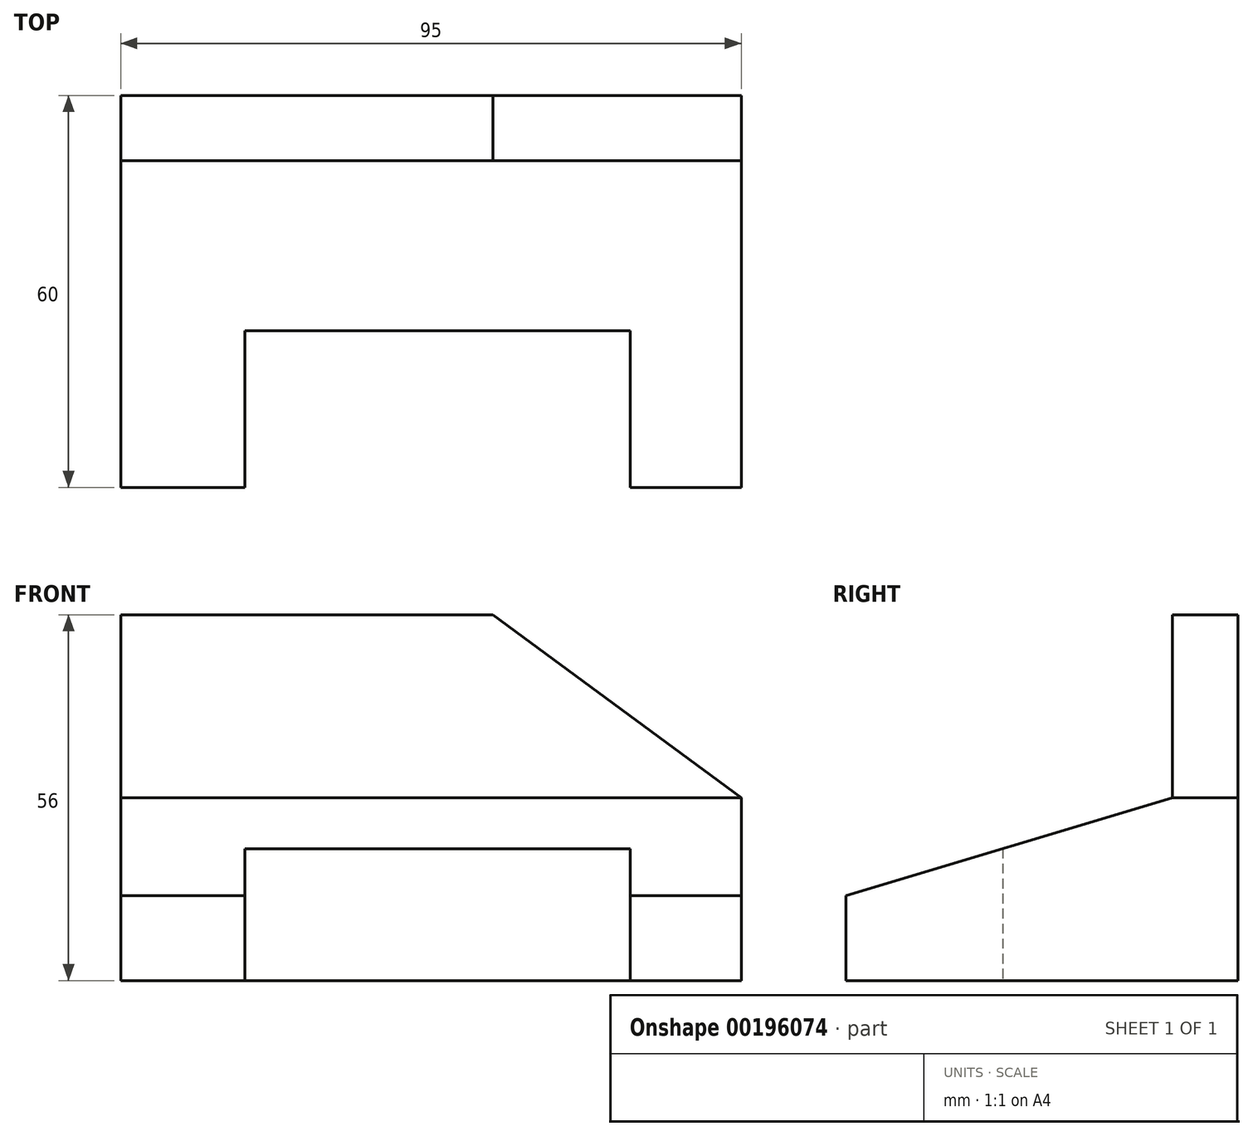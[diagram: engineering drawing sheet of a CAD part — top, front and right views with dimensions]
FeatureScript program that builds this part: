
annotation { "Feature Type Name" : "Feature", "Feature Type Description" : "" }
export const myFeature = defineFeature(function(context is Context, id is Id, definition is map)
    precondition{}
    {
        {
            var Q0;
            Q0=qCreatedBy(makeId("Right.planeOp"),FACE);
            var sketch = newSketch(context, id + "F0", { "sketchPlane" : qUnion([Q0])});
            skLineSegment(sketch, "E0", {"start": v(0, 0) * mm, "end": v(0, 56) * mm});
            skLineSegment(sketch, "E1", {"start": v(0, 56) * mm, "end": v(-10, 56) * mm});
            skLineSegment(sketch, "E2", {"start": v(-10, 56) * mm, "end": v(-10, 28) * mm});
            skLineSegment(sketch, "E3", {"start": v(-10, 28) * mm, "end": v(-60, 13) * mm});
            skLineSegment(sketch, "E4", {"start": v(-60, 13) * mm, "end": v(-60, 0) * mm});
            skLineSegment(sketch, "E5", {"start": v(-60, 0) * mm, "end": v(0, 0) * mm});
            skSolve(sketch);
        }
        {
            var Q0;
            Q0 = qSketchRegion(id + "F0", true);
            extrude(context, id + "F1", {"entities" : qUnion([Q0]), "depth" : 95 * mm});
        }
        {
            var Q0;
            Q0=makeQuery(id+"F1.opExtrude","SWEPT_FACE",FACE,{"disambiguationData":[OSD([sQuery(id+"F0.wireOp",EDGE,"E2")])]});
            var sketch = newSketch(context, id + "F2", { "sketchPlane" : qUnion([Q0])});
            skLineSegment(sketch, "E6", {"start": v(57, 56) * mm, "end": v(95, 28) * mm});
            skSolve(sketch);
        }
        {
            var Q0;
            {var subQ0=sQuery(id+"F2.wireOp",EDGE,"E6");Q0=makeQuery(id+"F2.imprint","IMPRINT",FACE,{"disambiguationData":[TD([[makeQuery(id+"F2.imprint","IMPRINT",EDGE,{"derivedFrom":subQ0}),1.0]])]});}
            var Q1;
            Q1=makeQuery(id+"F1.opExtrude","SWEPT_FACE",FACE,{"disambiguationData":[OSD([sQuery(id+"F0.wireOp",EDGE,"E0")])]});
            var Q2;
            Q2=makeQuery(id+"F1.opExtrude","SWEPT_BODY",BODY,{"disambiguationData":[OSD([sQuery(id+"F0.wireOp",EDGE,"E0"),sQuery(id+"F0.wireOp",EDGE,"E1"),sQuery(id+"F0.wireOp",EDGE,"E2"),sQuery(id+"F0.wireOp",EDGE,"E3"),sQuery(id+"F0.wireOp",EDGE,"E4"),sQuery(id+"F0.wireOp",EDGE,"E5")])]});
            var Q3;
            Q3=makeQuery(id+"F1.opExtrude","CAP_VERTEX",VERTEX,{"disambiguationData":[OSD([sQuery(id+"F0.wireOp",EDGE,"E0"),sQuery(id+"F0.wireOp",EDGE,"E5")])],"isStart":false});
            extrude(context, id + "F3", {"entities" : qUnion([Q0]), "operationType" : NewBodyOperationType.REMOVE, "endBound" : BoundingType.THROUGH_ALL, "oppositeDirection" : true, "endBoundEntityFace" : qUnion([Q1]), "endBoundEntityBody" : qUnion([Q2]), "endBoundEntityVertex" : qUnion([Q3]), "depth" : 25 * mm});
        }
        {
            var Q0;
            Q0=makeQuery(id+"F1.opExtrude","SWEPT_FACE",FACE,{"disambiguationData":[OSD([sQuery(id+"F0.wireOp",EDGE,"E5")])]});
            var sketch = newSketch(context, id + "F4", { "sketchPlane" : qUnion([Q0])});
            skLineSegment(sketch, "E7.bottom", {"start": v(78, 60) * mm, "end": v(19, 60) * mm});
            skLineSegment(sketch, "E7.top", {"start": v(78, 36) * mm, "end": v(19, 36) * mm});
            skLineSegment(sketch, "E7.left", {"start": v(78, 60) * mm, "end": v(78, 36) * mm});
            skLineSegment(sketch, "E7.right", {"start": v(19, 60) * mm, "end": v(19, 36) * mm});
            skSolve(sketch);
        }
        {
            var Q0;
            Q0=makeQuery(id+"F4.imprint","IMPRINT",FACE,{"disambiguationData":[TD([[makeQuery(id+"F4.imprint","IMPRINT",EDGE,{"derivedFrom":sQuery(id+"F4.wireOp",EDGE,"E7.bottom")}),1.0]])]});
            extrude(context, id + "F5", {"entities" : qUnion([Q0]), "operationType" : NewBodyOperationType.REMOVE, "endBound" : BoundingType.THROUGH_ALL, "oppositeDirection" : true, "depth" : 25 * mm});
        }
    });
